# Revit family: Legrand Export Snap on Columns accessoiries
name_source: partatom
category: Installations électriques
units: mm (PartAtom-declared; Revit-internal decimal feet)

## family parameters
Conserver l'orientation des annotations = Non
Cote de connecteur circulaire = Utiliser le diamètre
Couper avec des vides une fois chargée = Non
Hôte = Face
Partagée = Non
Point de calcul de pièce = Non
Type d'élément = Normal

## types (4) — shared parameters
Fabricant = LEGRAND
Standard = Snap-on-ON

## per-type parameters (varying)
| type | Accessoire | Description | Elévation par défaut | Finishing | Main Material | Modèle |
| Panel indicator | INFORMATIONS_PANEL_45 : 150x150mm | panel indicator 150x150mm cv45 | 2000 mm  [stored 6.56168 ft] | Mixed | Mixed | LG-653080 |
| Support TV screen 26 inches | TV_SUPPORT_45 : 25-66cm | tv Column mount 10-26 inch / 25-66cm / vesa. Column cv 45 mm | 1800 mm  [stored 5.90551 ft] | Mixed | Mixed | LG-653081 |
| Support TV screen 42 inches | TV_SUPPORT_45 : 66-107cm | tv Column mount 26-42 inch / 66-107cm / vesa. Column cv 45 mm | 1800 mm  [stored 5.90551 ft] | Mixed | Mixed | LG-653082 |
| Shelf | TABLES_45 : Shelf | shelf for cv45mm direct clipping Column | 900 mm  [stored 2.95276 ft] | White | Corian | LG-653083 |

note: [stored X ft] marks values corroborated as IEEE doubles in the binary element streams (Revit-internal decimal feet)
